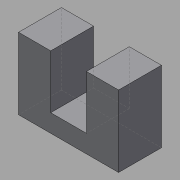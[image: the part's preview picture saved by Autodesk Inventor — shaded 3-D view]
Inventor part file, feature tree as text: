
AUTODESK INVENTOR PART (.ipt)
format: ipt  version: 2015 (Build 190159000, 159)  size: 77,312 bytes
history: native  units: in
note: dims shown in document units (in); Inventor stores cm internally (conversion verified against a paired STEP export)
features: other x3, sketch x2
ambient origin geometry x8: Origin, YZ Plane, XZ Plane, XY Plane, X Axis, Y Axis, Z Axis, Center Point
bodies: Solid1 (feature_tree)
feature tree (5):
  other  "opto_MIR1.ipt"
  other  "Solid1::opto_MIR1.ipt"
  other  "TaggingFeature1"
  sketch  "Sketch1"  dims[d0=0.3937in]
  sketch  "Sketch2"
